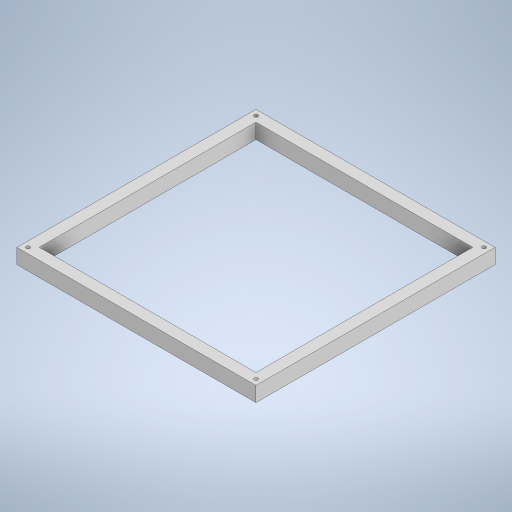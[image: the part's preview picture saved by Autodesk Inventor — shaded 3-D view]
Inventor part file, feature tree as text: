
AUTODESK INVENTOR PART (.ipt)
format: ipt  version: 2024 (Build 280153000, 153)  size: 278,528 bytes
history: native  units: in
note: dims shown in document units (in); Inventor stores cm internally (conversion verified against a paired STEP export)
features: extrude x2, projected_geometry x2
ambient origin geometry x8: Origin, YZ Plane, XZ Plane, XY Plane, X Axis, Y Axis, Z Axis, Center Point
bodies: Solid1 (feature_tree)
feature tree (4):
  extrude  "Extrusion1"  Depth=4.0in
  extrude  "Extrusion2"  Depth=4.0in
  projected_geometry  "Projected Loop1"
  projected_geometry  "Projected Loop2"
